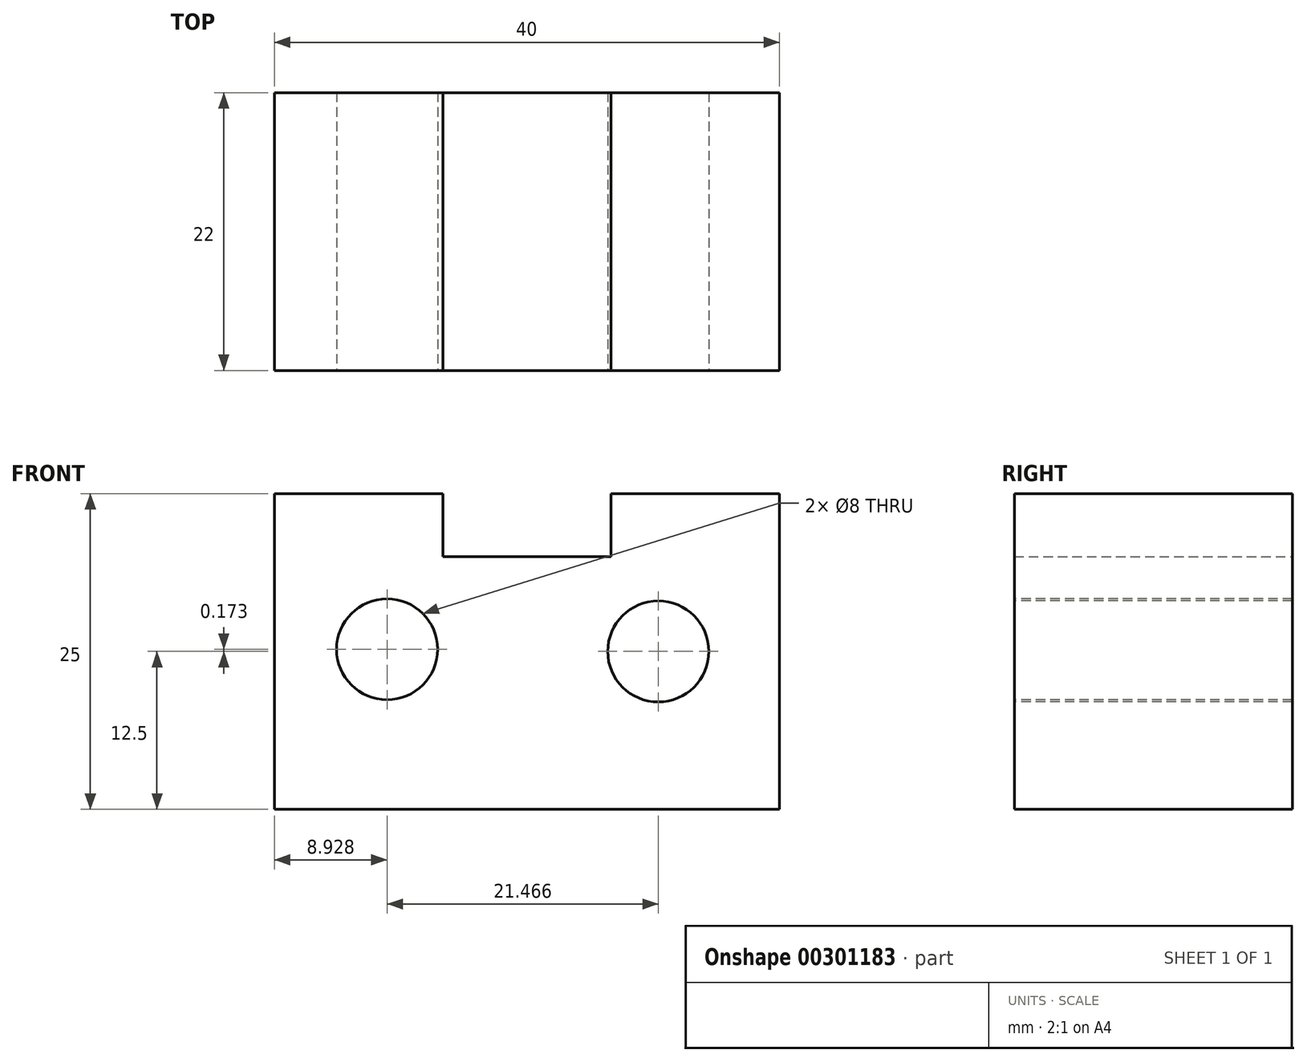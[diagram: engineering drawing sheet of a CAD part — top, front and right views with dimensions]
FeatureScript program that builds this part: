
annotation { "Feature Type Name" : "Feature", "Feature Type Description" : "" }
export const myFeature = defineFeature(function(context is Context, id is Id, definition is map)
    precondition{}
    {
        {
            var Q0;
            Q0=qCreatedBy(makeId("Front.planeOp"),FACE);
            var sketch = newSketch(context, id + "F0", { "sketchPlane" : qUnion([Q0])});
            skLineSegment(sketch, "E0", {"start": v(0, 0) * mm, "end": v(0, 25) * mm});
            skLineSegment(sketch, "E1", {"start": v(0, 0) * mm, "end": v(40, 0) * mm});
            skLineSegment(sketch, "E2", {"start": v(40, 0) * mm, "end": v(40, 25) * mm});
            skLineSegment(sketch, "E3", {"start": v(40, 25) * mm, "end": v(26.67, 25) * mm});
            skLineSegment(sketch, "E4", {"start": v(26.67, 25) * mm, "end": v(26.67, 20) * mm});
            skLineSegment(sketch, "E5", {"start": v(26.67, 20) * mm, "end": v(13.33, 20) * mm});
            skLineSegment(sketch, "E6", {"start": v(13.33, 20) * mm, "end": v(13.33, 25) * mm});
            skLineSegment(sketch, "E7", {"start": v(13.33, 25) * mm, "end": v(0, 25) * mm});
            skSolve(sketch);
        }
        {
            var Q0;
            Q0=makeQuery(id+"F0.imprint","IMPRINT",FACE,{"disambiguationData":[TD([[makeQuery(id+"F0.imprint","IMPRINT",EDGE,{"derivedFrom":sQuery(id+"F0.wireOp",EDGE,"E0")}),-1.0]])]});
            extrude(context, id + "F1", {"entities" : qUnion([Q0]), "depth" : 22 * mm});
        }
        {
            var Q0;
            Q0=makeQuery(id+"F1.opExtrude","CAP_FACE",FACE,{"disambiguationData":[OSD([sQuery(id+"F0.wireOp",EDGE,"E0"),sQuery(id+"F0.wireOp",EDGE,"E1"),sQuery(id+"F0.wireOp",EDGE,"E2"),sQuery(id+"F0.wireOp",EDGE,"E3"),sQuery(id+"F0.wireOp",EDGE,"E4"),sQuery(id+"F0.wireOp",EDGE,"E5"),sQuery(id+"F0.wireOp",EDGE,"E6"),sQuery(id+"F0.wireOp",EDGE,"E7")])],"isStart":false});
            var sketch = newSketch(context, id + "F2", { "sketchPlane" : qUnion([Q0])});
            skLineSegment(sketch, "E8", {"start": v(0, 12.5) * mm, "end": v(5, 12.5) * mm});
            skLineSegment(sketch, "E9", {"start": v(40, 12.5) * mm, "end": v(35, 12.5) * mm});
            skLineSegment(sketch, "E10", {"start": v(8.32, 0) * mm, "end": v(8.32, 8) * mm});
            skLineSegment(sketch, "E11", {"start": v(31.2, 0) * mm, "end": v(31.2, 8) * mm});
            skLineSegment(sketch, "E12", {"start": v(6.67, 25) * mm, "end": v(6.67, 17) * mm});
            skPoint(sketch, "E12.endSnap0", {"position": v(6.67, 25) * mm});
            skPoint(sketch, "E13", {"position": v(8.93, 12.67) * mm});
            skSolve(sketch);
        }
        {
            var Q0;
            Q0=sQuery(id+"F2.wireOp",VERTEX,"E13");
            var Q1;
            Q1=makeQuery(id+"F1.opExtrude","SWEPT_BODY",BODY,{"disambiguationData":[OSD([sQuery(id+"F0.wireOp",EDGE,"E0"),sQuery(id+"F0.wireOp",EDGE,"E1"),sQuery(id+"F0.wireOp",EDGE,"E2"),sQuery(id+"F0.wireOp",EDGE,"E3"),sQuery(id+"F0.wireOp",EDGE,"E4"),sQuery(id+"F0.wireOp",EDGE,"E5"),sQuery(id+"F0.wireOp",EDGE,"E6"),sQuery(id+"F0.wireOp",EDGE,"E7")])]});
            hole(context, id + "F3", {"style" : HoleStyle.SIMPLE, "endStyle" : HoleEndStyle.THROUGH, "holeDiameter" : 8 * mm, "tappedDepth" : 12 * mm, "tapClearance" : 3, "locations" : qUnion([Q0]), "scope" : qUnion([Q1])});
        }
        {
            var Q0;
            Q0=makeQuery(id+"F1.opExtrude","CAP_FACE",FACE,{"disambiguationData":[OSD([sQuery(id+"F0.wireOp",EDGE,"E0"),sQuery(id+"F0.wireOp",EDGE,"E1"),sQuery(id+"F0.wireOp",EDGE,"E2"),sQuery(id+"F0.wireOp",EDGE,"E3"),sQuery(id+"F0.wireOp",EDGE,"E4"),sQuery(id+"F0.wireOp",EDGE,"E5"),sQuery(id+"F0.wireOp",EDGE,"E6"),sQuery(id+"F0.wireOp",EDGE,"E7")])],"isStart":false});
            var sketch = newSketch(context, id + "F4", { "sketchPlane" : qUnion([Q0])});
            skLineSegment(sketch, "E14", {"start": v(12.93, 12.66) * mm, "end": v(25.93, 12.66) * mm});
            skLineSegment(sketch, "E15", {"start": v(7.88, 16.53) * mm, "end": v(40, 16.53) * mm});
            skLineSegment(sketch, "E16", {"start": v(7.54, 8.92) * mm, "end": v(40, 8.92) * mm});
            skLineSegment(sketch, "E17", {"start": v(40, 12.5) * mm, "end": v(35.07, 12.5) * mm});
            skPoint(sketch, "E18", {"position": v(30.4, 12.5) * mm});
            skSolve(sketch);
        }
        {
            var Q0;
            Q0=sQuery(id+"F4.wireOp",VERTEX,"E18");
            var Q1;
            Q1=makeQuery(id+"F1.opExtrude","SWEPT_BODY",BODY,{"disambiguationData":[OSD([sQuery(id+"F0.wireOp",EDGE,"E0"),sQuery(id+"F0.wireOp",EDGE,"E1"),sQuery(id+"F0.wireOp",EDGE,"E2"),sQuery(id+"F0.wireOp",EDGE,"E3"),sQuery(id+"F0.wireOp",EDGE,"E4"),sQuery(id+"F0.wireOp",EDGE,"E5"),sQuery(id+"F0.wireOp",EDGE,"E6"),sQuery(id+"F0.wireOp",EDGE,"E7")])]});
            hole(context, id + "F5", {"style" : HoleStyle.SIMPLE, "endStyle" : HoleEndStyle.THROUGH, "holeDiameter" : 8 * mm, "tappedDepth" : 12 * mm, "tapClearance" : 3, "locations" : qUnion([Q0]), "scope" : qUnion([Q1])});
        }
    });
